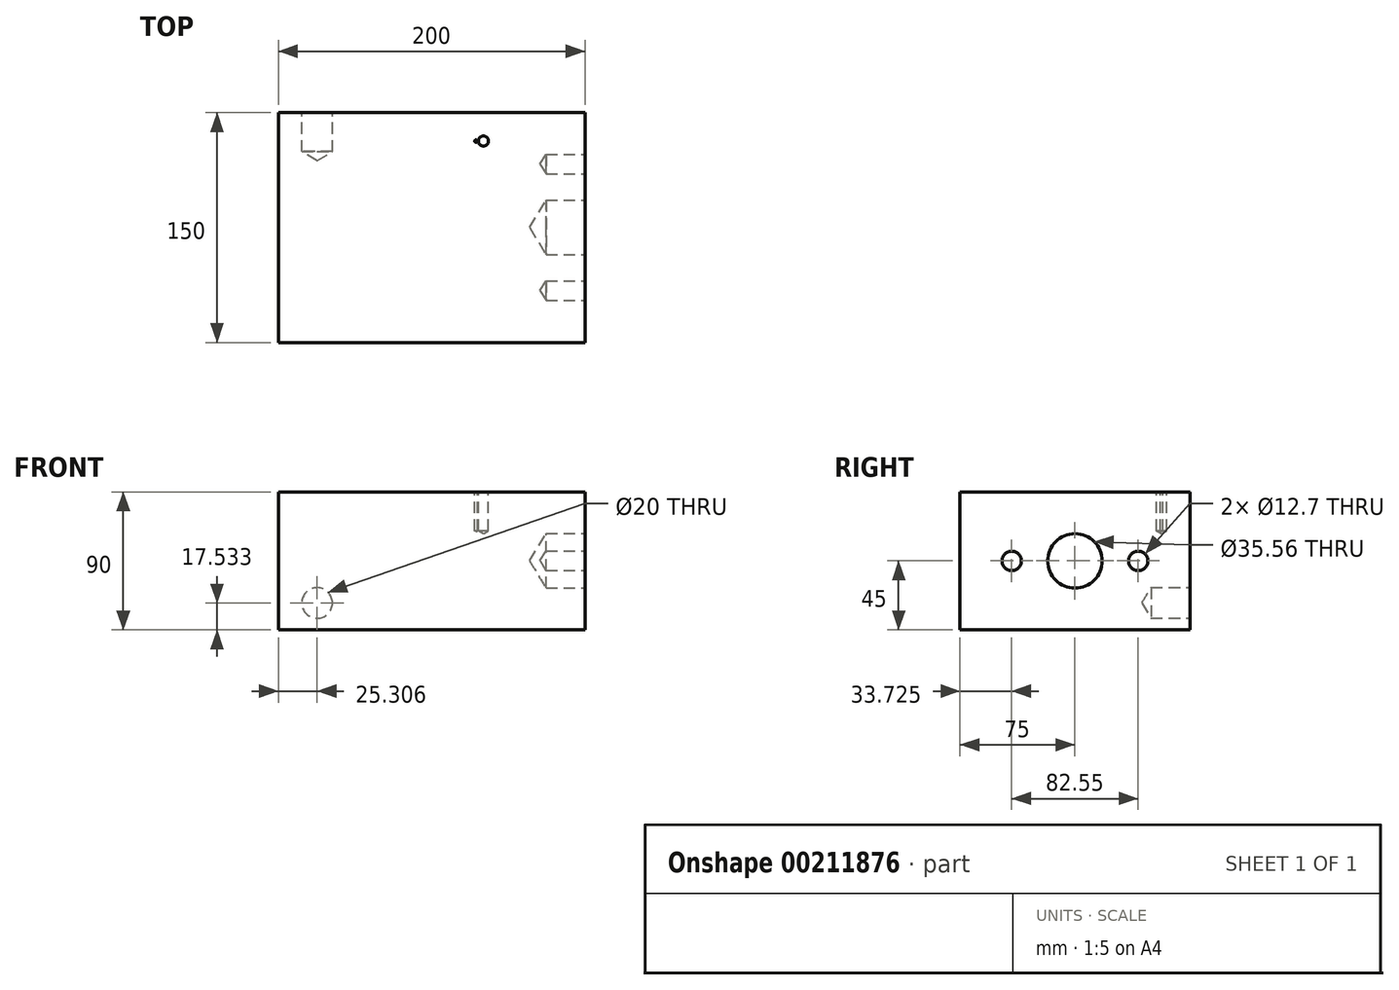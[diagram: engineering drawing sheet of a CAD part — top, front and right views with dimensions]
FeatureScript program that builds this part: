
annotation { "Feature Type Name" : "Feature", "Feature Type Description" : "" }
export const myFeature = defineFeature(function(context is Context, id is Id, definition is map)
    precondition{}
    {
        {
            var Q0;
            Q0=qCreatedBy(makeId("Top.planeOp"),FACE);
            var sketch = newSketch(context, id + "F0", { "sketchPlane" : qUnion([Q0])});
            skLineSegment(sketch, "E0.bottom", {"start": v(-100, 75) * mm, "end": v(100, 75) * mm});
            skLineSegment(sketch, "E0.top", {"start": v(-100, -75) * mm, "end": v(100, -75) * mm});
            skLineSegment(sketch, "E0.left", {"start": v(-100, 75) * mm, "end": v(-100, -75) * mm});
            skLineSegment(sketch, "E0.right", {"start": v(100, 75) * mm, "end": v(100, -75) * mm});
            skPoint(sketch, "E0.middle", {"position": v(0, 0) * mm});
            skSolve(sketch);
        }
        {
            var Q0;
            Q0=makeQuery(id+"F0.imprint","IMPRINT",FACE,{"disambiguationData":[TD([[makeQuery(id+"F0.imprint","IMPRINT",EDGE,{"derivedFrom":sQuery(id+"F0.wireOp",EDGE,"E0.bottom")}),-1.0]])]});
            extrude(context, id + "F1", {"entities" : qUnion([Q0]), "endBound" : BoundingType.SYMMETRIC, "depth" : 90 * mm});
        }
        {
            var Q0;
            Q0=makeQuery(id+"F1.opExtrude","SWEPT_FACE",FACE,{"disambiguationData":[OSD([sQuery(id+"F0.wireOp",EDGE,"E0.right")])]});
            var sketch = newSketch(context, id + "F2", { "sketchPlane" : qUnion([Q0])});
            skSolve(sketch);
        }
        {
            var Q0;
            Q0=makeQuery(id+"F1.opExtrude","SWEPT_FACE",FACE,{"disambiguationData":[OSD([sQuery(id+"F0.wireOp",EDGE,"E0.bottom")])]});
            var sketch = newSketch(context, id + "F3", { "sketchPlane" : qUnion([Q0])});
            skCircle(sketch, "E1", {"center": v(74.7, -27.47) * mm, "radius": 10 * mm});
            skSolve(sketch);
        }
        {
            var Q0;
            Q0=makeQuery(id+"F1.opExtrude","CAP_FACE",FACE,{"disambiguationData":[OSD([sQuery(id+"F0.wireOp",EDGE,"E0.bottom"),sQuery(id+"F0.wireOp",EDGE,"E0.top"),sQuery(id+"F0.wireOp",EDGE,"E0.left"),sQuery(id+"F0.wireOp",EDGE,"E0.right")])],"isStart":false});
            var sketch = newSketch(context, id + "F4", { "sketchPlane" : qUnion([Q0])});
            skCircle(sketch, "E2", {"center": v(33.8, 56.44) * mm, "radius": 3.28 * mm});
            skCircle(sketch, "E3", {"center": v(29.02, 56.44) * mm, "radius": 0.87 * mm});
            skSolve(sketch);
        }
        {
            var Q0;
            {var subQ0=sQuery(id+"F0.wireOp",EDGE,"E0.right");Q0=makeQuery(id+"F2.imprint","IMPRINT",FACE,{"disambiguationData":[TD([[makeQuery(id+"F2.imprint","IMPRINT",EDGE,{"derivedFrom":makeQuery(id+"F1.opExtrude","CAP_EDGE",EDGE,{"disambiguationData":[OSD([subQ0])],"isStart":true})}),-1.0]])]});}
            var sketch = newSketch(context, id + "F5", { "sketchPlane" : qUnion([Q0])});
            skCircle(sketch, "E4", {"center": v(0, 0) * mm, "radius": 18.03 * mm});
            skCircle(sketch, "E5", {"center": v(-41.28, 0) * mm, "radius": 6.35 * mm});
            skCircle(sketch, "E6", {"center": v(41.28, 0) * mm, "radius": 6.35 * mm});
            skSolve(sketch);
        }
        {
            var Q0;
            Q0=sQuery(id+"F5.wireOp",VERTEX,"E5.center");
            var Q1;
            Q1=makeQuery(id+"F1.opExtrude","SWEPT_BODY",BODY,{"disambiguationData":[OSD([sQuery(id+"F0.wireOp",EDGE,"E0.bottom"),sQuery(id+"F0.wireOp",EDGE,"E0.top"),sQuery(id+"F0.wireOp",EDGE,"E0.left"),sQuery(id+"F0.wireOp",EDGE,"E0.right")])]});
            hole(context, id + "F6", {"style" : HoleStyle.SIMPLE, "endStyle" : HoleEndStyle.BLIND, "holeDiameter" : 12.7 * mm, "holeDepth" : 25.4 * mm, "locations" : qUnion([Q0]), "scope" : qUnion([Q1])});
        }
        {
            var Q0;
            Q0=sQuery(id+"F5.wireOp",VERTEX,"E6.center");
            var Q1;
            Q1=makeQuery(id+"F1.opExtrude","SWEPT_BODY",BODY,{"disambiguationData":[OSD([sQuery(id+"F0.wireOp",EDGE,"E0.bottom"),sQuery(id+"F0.wireOp",EDGE,"E0.top"),sQuery(id+"F0.wireOp",EDGE,"E0.left"),sQuery(id+"F0.wireOp",EDGE,"E0.right")])]});
            hole(context, id + "F7", {"style" : HoleStyle.SIMPLE, "endStyle" : HoleEndStyle.BLIND, "holeDiameter" : 12.7 * mm, "holeDepth" : 25.4 * mm, "locations" : qUnion([Q0]), "scope" : qUnion([Q1])});
        }
        {
            var Q0;
            Q0=sQuery(id+"F5.wireOp",VERTEX,"E4.center");
            var Q1;
            Q1=makeQuery(id+"F1.opExtrude","SWEPT_BODY",BODY,{"disambiguationData":[OSD([sQuery(id+"F0.wireOp",EDGE,"E0.bottom"),sQuery(id+"F0.wireOp",EDGE,"E0.top"),sQuery(id+"F0.wireOp",EDGE,"E0.left"),sQuery(id+"F0.wireOp",EDGE,"E0.right")])]});
            hole(context, id + "F8", {"style" : HoleStyle.SIMPLE, "endStyle" : HoleEndStyle.BLIND, "holeDiameter" : 35.56 * mm, "holeDepth" : 25.4 * mm, "locations" : qUnion([Q0]), "scope" : qUnion([Q1])});
        }
        {
            var Q0;
            Q0=sQuery(id+"F4.wireOp",VERTEX,"E2.center");
            var Q1;
            Q1=makeQuery(id+"F1.opExtrude","SWEPT_BODY",BODY,{"disambiguationData":[OSD([sQuery(id+"F0.wireOp",EDGE,"E0.bottom"),sQuery(id+"F0.wireOp",EDGE,"E0.top"),sQuery(id+"F0.wireOp",EDGE,"E0.left"),sQuery(id+"F0.wireOp",EDGE,"E0.right")])]});
            hole(context, id + "F9", {"style" : HoleStyle.SIMPLE, "endStyle" : HoleEndStyle.BLIND, "holeDiameter" : 6.56 * mm, "holeDepth" : 25.4 * mm, "locations" : qUnion([Q0]), "scope" : qUnion([Q1])});
        }
        {
            var Q0;
            Q0=sQuery(id+"F4.wireOp",VERTEX,"E3.center");
            var Q1;
            Q1=makeQuery(id+"F1.opExtrude","SWEPT_BODY",BODY,{"disambiguationData":[OSD([sQuery(id+"F0.wireOp",EDGE,"E0.bottom"),sQuery(id+"F0.wireOp",EDGE,"E0.top"),sQuery(id+"F0.wireOp",EDGE,"E0.left"),sQuery(id+"F0.wireOp",EDGE,"E0.right")])]});
            hole(context, id + "F10", {"style" : HoleStyle.SIMPLE, "endStyle" : HoleEndStyle.BLIND, "holeDiameter" : 1.73 * mm, "holeDepth" : 25.4 * mm, "locations" : qUnion([Q0]), "scope" : qUnion([Q1])});
        }
        {
            var Q0;
            Q0=sQuery(id+"F3.wireOp",VERTEX,"E1.center");
            var Q1;
            Q1=makeQuery(id+"F1.opExtrude","SWEPT_BODY",BODY,{"disambiguationData":[OSD([sQuery(id+"F0.wireOp",EDGE,"E0.bottom"),sQuery(id+"F0.wireOp",EDGE,"E0.top"),sQuery(id+"F0.wireOp",EDGE,"E0.left"),sQuery(id+"F0.wireOp",EDGE,"E0.right")])]});
            hole(context, id + "F11", {"style" : HoleStyle.SIMPLE, "endStyle" : HoleEndStyle.BLIND, "holeDiameter" : 20 * mm, "holeDepth" : 25.4 * mm, "locations" : qUnion([Q0]), "scope" : qUnion([Q1])});
        }
    });
